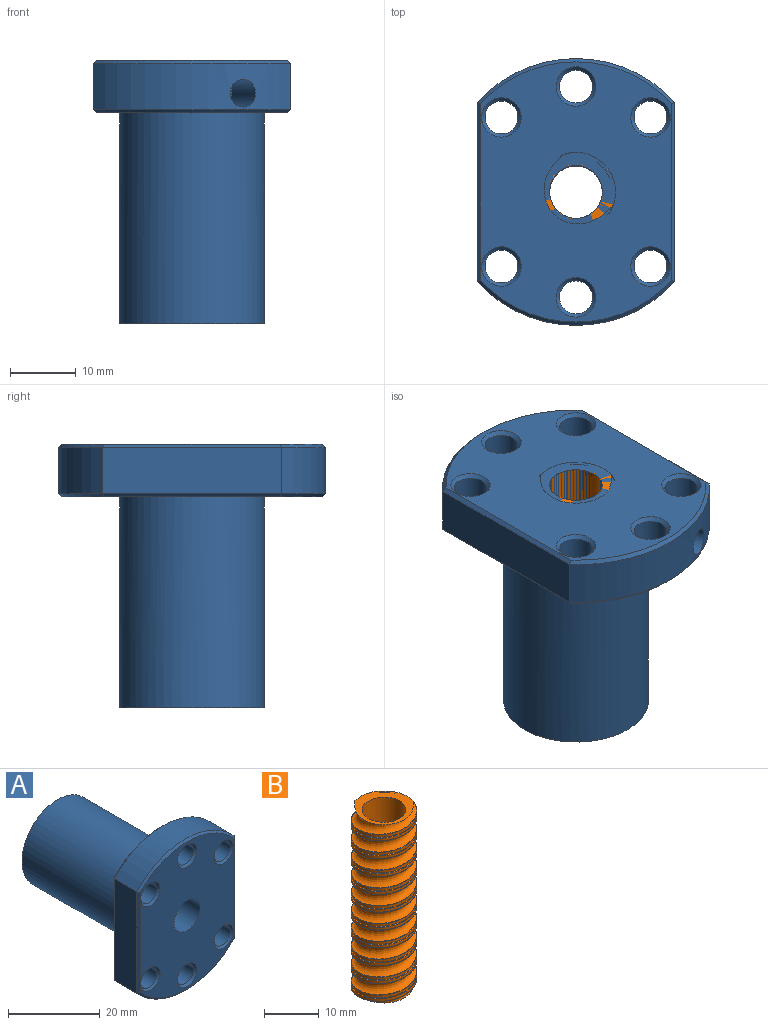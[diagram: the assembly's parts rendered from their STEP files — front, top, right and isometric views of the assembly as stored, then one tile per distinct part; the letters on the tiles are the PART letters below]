
ASSEMBLY  parts=2 mates=1
PART A: 37 faces, bbox 30x40x40.5 mm
  f0: plane 39.5x29mm, normal (0,-1,0), area 812.1mm2, adj f14,f15,f16,f17,f18,f19,f20,f21
  f1: plane 39.5x29mm, normal (0,1,0), area 482.3mm2, adj f6,f24,f25,f26,f27,f28,f29,f30
  f2: cylinder r=20.25mm len=30mm, axis (0,-1,0), area 222.6mm2, adj f3,f5,f13,f20,f32
  f3: plane 27.21x7mm, normal (-1,0,0), area 190.5mm2, adj f2,f4,f22,f30
  f4: cylinder r=20.25mm len=30mm, axis (0,-1,0), area 236.5mm2, adj f3,f5,f21,f31
  f5: plane 27.21x7mm, normal (1,0,0), area 190.5mm2, adj f2,f4,f19,f33
  f6: cylinder r=11mm len=32mm, axis (0,-1,0), area 2211.7mm2, adj f1,f34
  f7: cylinder r=2.5mm len=7mm, axis (0,-1,0), area 110mm2, adj f18,f24
  f8: cylinder r=2.5mm len=7mm, axis (0,-1,0), area 110mm2, adj f17,f25
  f9: cylinder r=2.5mm len=7mm, axis (0,-1,0), area 110mm2, adj f16,f26
  f10: cylinder r=2.5mm len=7mm, axis (0,-1,0), area 110mm2, adj f15,f27
  f11: cylinder r=2.5mm len=7mm, axis (0,-1,0), area 110mm2, adj f14,f29
  f12: cylinder r=2.5mm len=7mm, axis (0,-1,0), area 110mm2, adj f23,f28
  f13: cylinder r=2.1mm len=10.34mm, axis (0.38,0,-0.92), area 122.7mm2, adj f2,f35
  f14: cone r=2.5mm half-angle=45deg, axis (0,-1,0), area 12.2mm2, adj f0,f11
  f15: cone r=2.5mm half-angle=45deg, axis (0,-1,0), area 12.2mm2, adj f0,f10
  f16: cone r=2.5mm half-angle=45deg, axis (0,-1,0), area 12.2mm2, adj f0,f9
  f17: cone r=2.5mm half-angle=45deg, axis (0,-1,0), area 12.2mm2, adj f0,f8
  f18: cone r=2.5mm half-angle=45deg, axis (0,-1,0), area 12.2mm2, adj f0,f7
  f19: plane 27.21x0.5mm, normal (0.71,-0.71,0), area 19.1mm2, adj f0,f5,f20,f21
  f20: cone r=20.25mm half-angle=45deg, axis (0,1,0), area 23.5mm2, adj f0,f2,f19,f22
  f21: cone r=20.25mm half-angle=45deg, axis (0,1,0), area 23.5mm2, adj f0,f4,f19,f22
  f22: plane 27.21x0.5mm, normal (-0.71,-0.71,0), area 19.1mm2, adj f0,f3,f20,f21
  f23: cone r=2.5mm half-angle=45deg, axis (0,-1,0), area 12.2mm2, adj f0,f12
  f24: cone r=2.5mm half-angle=45deg, axis (0,1,0), area 12.2mm2, adj f1,f7
  f25: cone r=2.5mm half-angle=45deg, axis (0,1,0), area 12.2mm2, adj f1,f8
  f26: cone r=2.5mm half-angle=45deg, axis (0,1,0), area 12.2mm2, adj f1,f9
  f27: cone r=2.5mm half-angle=45deg, axis (0,1,0), area 12.2mm2, adj f1,f10
  f28: cone r=2.5mm half-angle=45deg, axis (0,1,0), area 12.2mm2, adj f1,f12
  f29: cone r=2.5mm half-angle=45deg, axis (0,1,0), area 12.2mm2, adj f1,f11
  f30: plane 27.21x0.5mm, normal (-0.71,0.71,0), area 19.1mm2, adj f1,f3,f31,f32
  f31: cone r=19.75mm half-angle=45deg, axis (0,-1,0), area 23.5mm2, adj f1,f4,f30,f33
  f32: cone r=19.75mm half-angle=45deg, axis (0,-1,0), area 23.5mm2, adj f1,f2,f30,f33
  f33: plane 27.21x0.5mm, normal (0.71,0.71,0), area 19.1mm2, adj f1,f5,f31,f32
  f34: plane 22x22mm, normal (0,1,0), area 329.9mm2, adj f6,f36
  f35: cylinder r=11mm len=4.2mm, axis (0,-1,0), area 13.9mm2, adj f13
  f36: cylinder r=4mm len=40mm, axis (0,1,0), area 1005.3mm2, adj f0,f34
PART B: 11 faces, bbox 12x13.9x45.9 mm
  f0: bspline ~45.83x13.75mm, area 1253mm2, adj f1,f2,f8,f9
  f1: bspline ~40.72x13.86mm, area 28.9mm2, adj f0,f6,f8,f9
  f2: bspline ~40.72x13.86mm, area 28.9mm2, adj f0,f5,f8,f9
  f3: bspline ~40.67x13.86mm, area 181.8mm2, adj f5,f7,f8,f9
  f4: bspline ~40.67x13.86mm, area 181.6mm2, adj f6,f7,f8,f9
  f5: cylinder r=6mm len=40mm, axis (0,0,-1), area 179.9mm2, adj f2,f3,f8,f9
  f6: cylinder r=6mm len=40mm, axis (0,0,-1), area 261.1mm2, adj f1,f4,f8,f9
  f7: cylinder r=5.5mm len=40mm, axis (0,0,-1), area 93.3mm2, adj f3,f4,f8,f9
  f8: plane 10.9x10.9mm, normal (0,0,-1), area 40.8mm2, adj f0,f1,f2,f3,f4,f5,f6,f7
  f9: plane 10.9x10.9mm, normal (0,0,1), area 40.8mm2, adj f0,f1,f2,f3,f4,f5,f6,f7
  f10: cylinder r=4mm len=40mm, axis (0,0,1), area 1005.3mm2, adj f8,f9
PLACE A rot(axis=(-1,0,0),90deg) t=(12.38,0.22,36.8)mm
PLACE B t=(12.38,0.22,36.8)mm
MATE fastened A.f36 <-> B.f10  axis (0,0,1) through (12.38,0.22,36.8)mm
